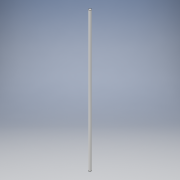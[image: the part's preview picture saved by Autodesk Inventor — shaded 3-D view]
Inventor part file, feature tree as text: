
AUTODESK INVENTOR PART (.ipt)
format: ipt  version: 2018 (Build 220112000, 112)  size: 94,208 bytes
history: native  units: in
note: dims shown in document units (in); Inventor stores cm internally (conversion verified against a paired STEP export)
features: revolve x1, sketch x1
ambient origin geometry x8: Origin, YZ Plane, XZ Plane, XY Plane, X Axis, Y Axis, Z Axis, Center Point
bodies: Solid1 (feature_tree)
feature tree (2):
  revolve  "Revolution1"  [1 undecoded]
  sketch  "Sketch1"  dims[d0=5.5118in d1=0.0492in d2=90.0deg]
note: 1 required parameter value undecoded (feature->parameter linkage not recoverable at this tier; creation-order binding heuristic only, values carry confidence <= 0.55)
